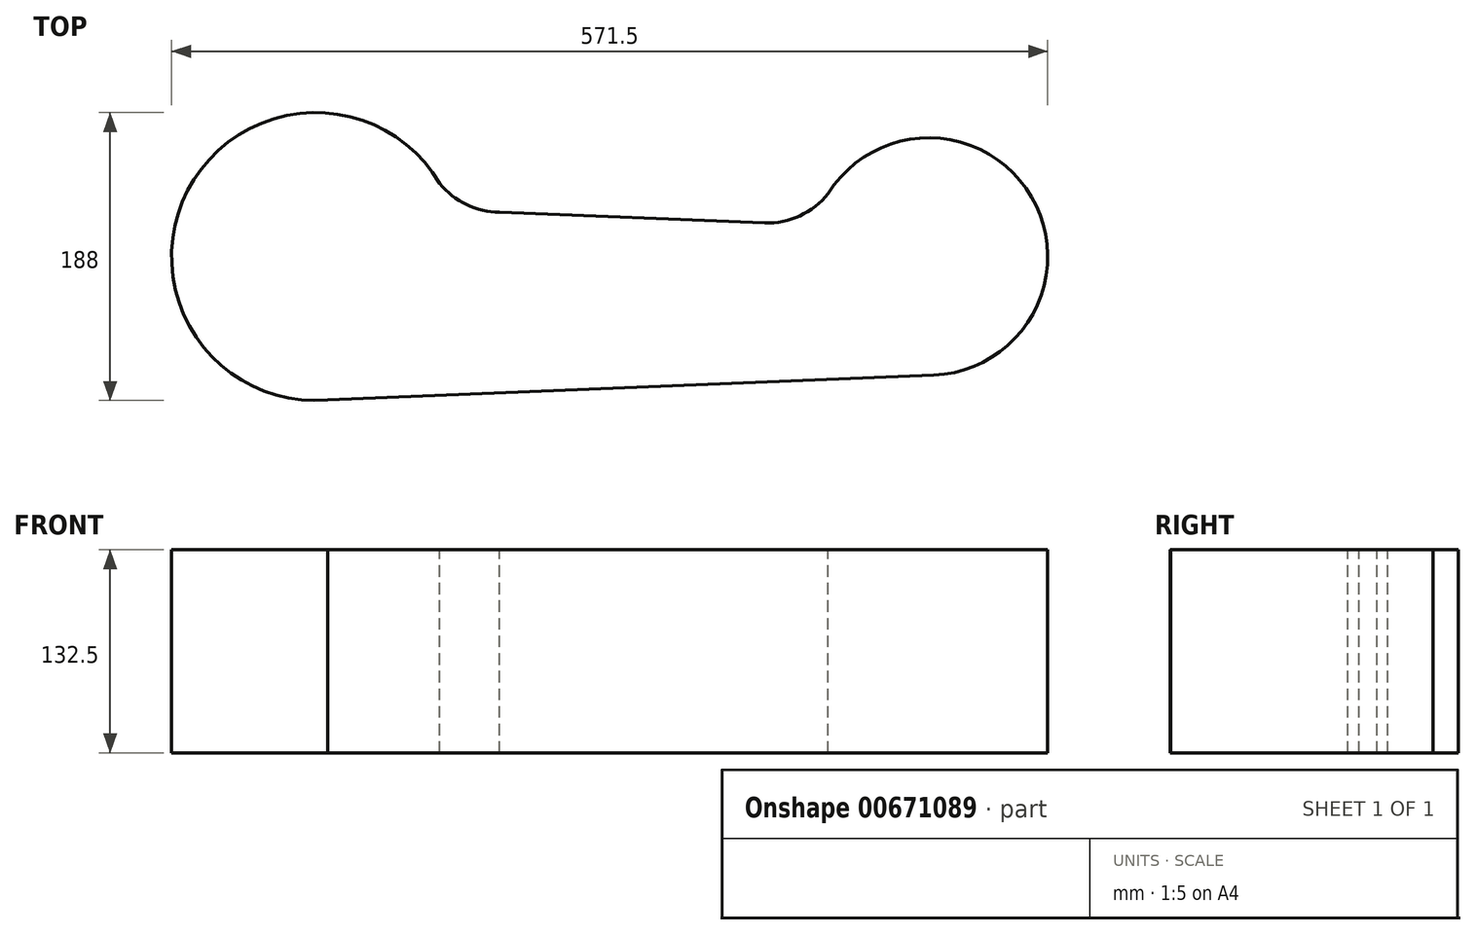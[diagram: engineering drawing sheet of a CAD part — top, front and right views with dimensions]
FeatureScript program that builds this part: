
annotation { "Feature Type Name" : "Feature", "Feature Type Description" : "" }
export const myFeature = defineFeature(function(context is Context, id is Id, definition is map)
    precondition{}
    {
        {
            var Q0;
            Q0=qCreatedBy(makeId("Top.planeOp"),FACE);
            var sketch = newSketch(context, id + "F0", { "sketchPlane" : qUnion([Q0])});
            skArc(sketch, "E0", {"start": v(80.97, 47.75) * mm, "mid": v(-83.47, 43.23) * mm, "end": v(7.71, -93.68) * mm});
            skArc(sketch, "E1", {"start": v(403.18, -77.43) * mm, "mid": v(466.98, 38.98) * mm, "end": v(334.25, 41.02) * mm});
            skArc(sketch, "E2", {"start": v(293, 22.04) * mm, "mid": v(318.9, 28.08) * mm, "end": v(338.04, 46.55) * mm});
            skArc(sketch, "E3", {"start": v(75.87, 55.5) * mm, "mid": v(94.26, 36.13) * mm, "end": v(120, 29) * mm});
            skLineSegment(sketch, "E4", {"start": v(120, 29) * mm, "end": v(295, 21.96) * mm});
            skLineSegment(sketch, "E5", {"start": v(0, -94) * mm, "end": v(403.18, -77.43) * mm});
            skSolve(sketch);
        }
        {
            var Q0;
            Q0 = qSketchRegion(id + "F0", true);
            extrude(context, id + "F1", {"entities" : qUnion([Q0]), "oppositeDirection" : true, "depth" : 132.5 * mm, "offsetDistance" : 25 * mm});
        }
    });
